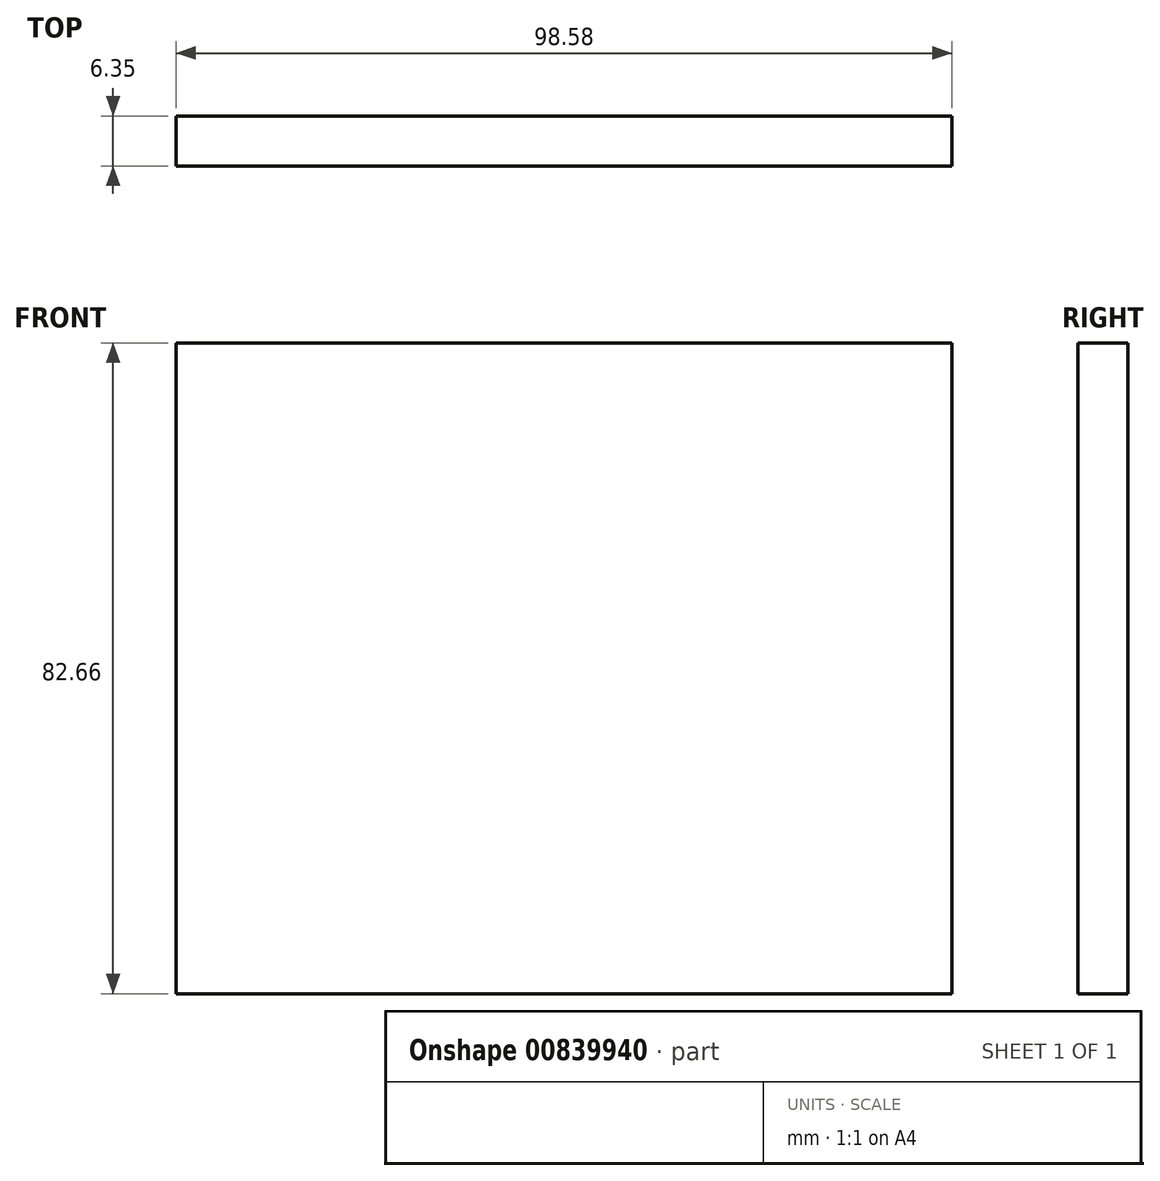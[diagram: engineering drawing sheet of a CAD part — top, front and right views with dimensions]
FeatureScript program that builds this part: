
annotation { "Feature Type Name" : "Feature", "Feature Type Description" : "" }
export const myFeature = defineFeature(function(context is Context, id is Id, definition is map)
    precondition{}
    {
        {
            var Q0;
            Q0=qCreatedBy(makeId("Front.planeOp"),FACE);
            var sketch = newSketch(context, id + "F0", { "sketchPlane" : qUnion([Q0])});
            skLineSegment(sketch, "E0.bottom", {"start": v(49.3, 41.33) * mm, "end": v(-49.3, 41.33) * mm});
            skLineSegment(sketch, "E0.top", {"start": v(49.3, -41.33) * mm, "end": v(-49.3, -41.33) * mm});
            skLineSegment(sketch, "E0.left", {"start": v(49.3, 41.33) * mm, "end": v(49.3, -41.33) * mm});
            skLineSegment(sketch, "E0.right", {"start": v(-49.3, 41.33) * mm, "end": v(-49.3, -41.33) * mm});
            skPoint(sketch, "E0.middle", {"position": v(0, 0) * mm});
            skSolve(sketch);
        }
        {
            var Q0;
            Q0 = qSketchRegion(id + "F0", true);
            extrude(context, id + "F1", {"entities" : qUnion([Q0]), "depth" : 6.35 * mm, "offsetDistance" : 25.4 * mm});
        }
    });
